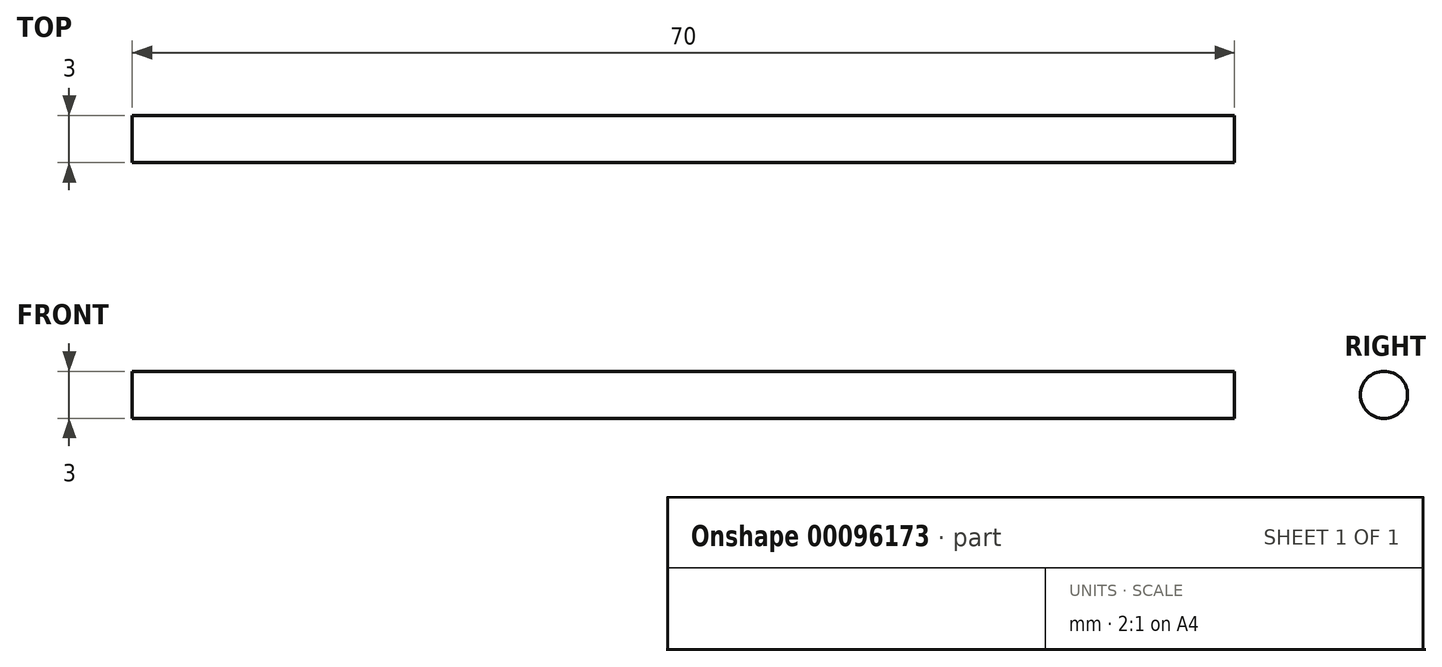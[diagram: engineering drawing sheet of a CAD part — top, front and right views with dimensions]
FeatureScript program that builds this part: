
annotation { "Feature Type Name" : "Feature", "Feature Type Description" : "" }
export const myFeature = defineFeature(function(context is Context, id is Id, definition is map)
    precondition{}
    {
        {
            var Q0;
            Q0=qCreatedBy(makeId("Right.planeOp"),FACE);
            var sketch = newSketch(context, id + "F0", { "sketchPlane" : qUnion([Q0])});
            skCircle(sketch, "E0", {"center": v(0, 0) * mm, "radius": 1.5 * mm});
            skSolve(sketch);
        }
        {
            var Q0;
            Q0=qSketchRegion(id+"F0",true);
            extrude(context, id + "F1", {"entities" : qUnion([Q0]), "depth" : 35 * mm, "hasSecondDirection" : true, "secondDirectionOppositeDirection" : true, "secondDirectionDepth" : 35 * mm});
        }
    });
